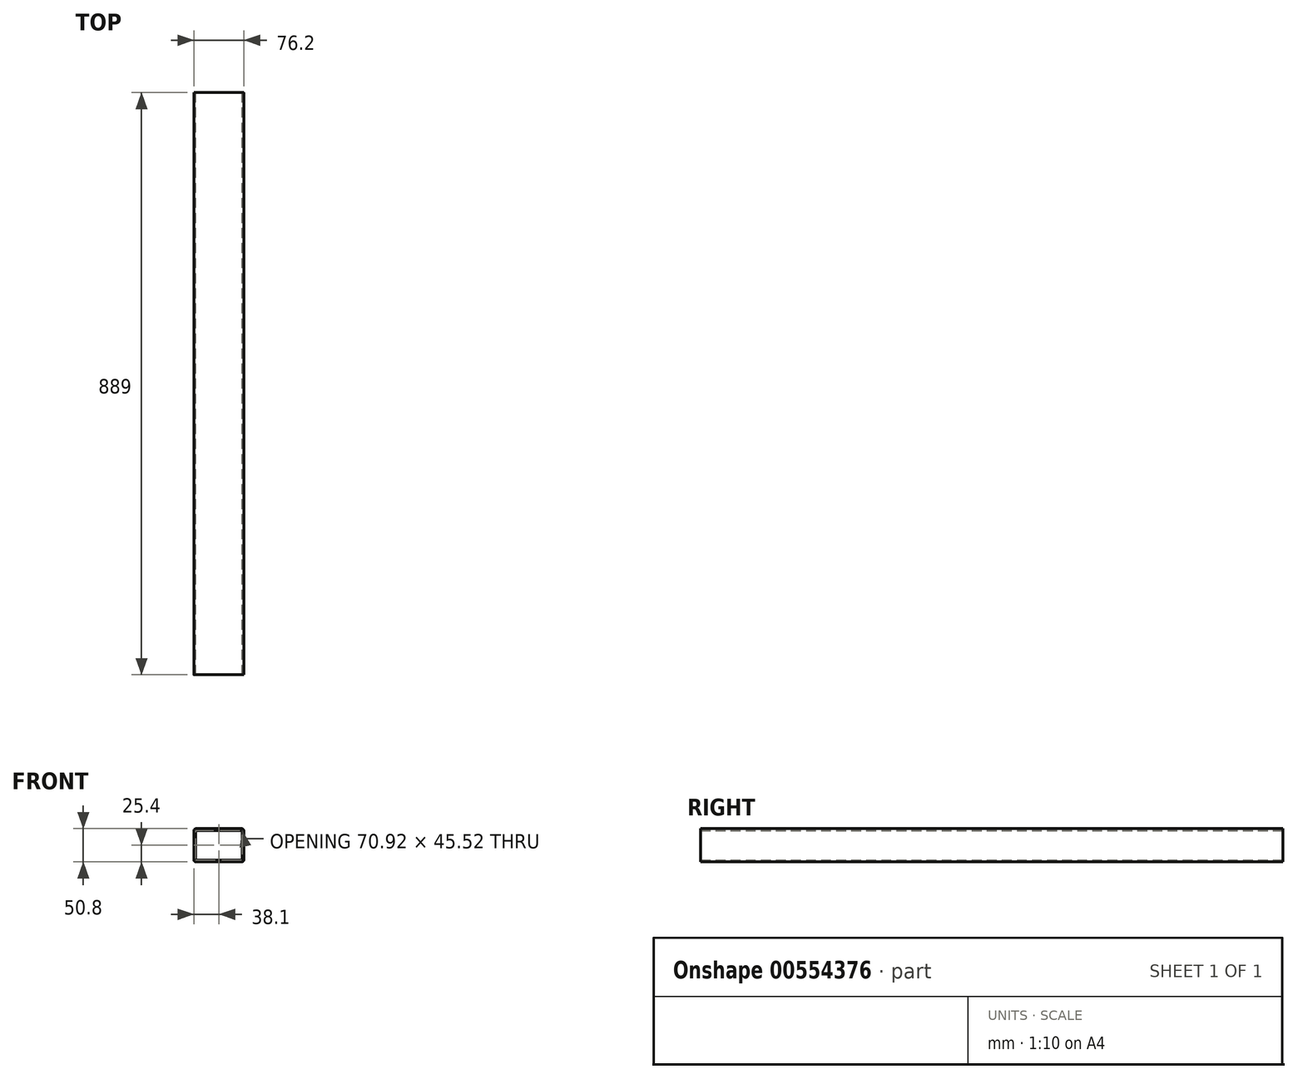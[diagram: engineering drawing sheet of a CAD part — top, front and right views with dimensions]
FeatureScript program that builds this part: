
annotation { "Feature Type Name" : "Feature", "Feature Type Description" : "" }
export const myFeature = defineFeature(function(context is Context, id is Id, definition is map)
    precondition{}
    {
        {
            var Q0;
            Q0=qCreatedBy(makeId("Front.planeOp"),FACE);
            var sketch = newSketch(context, id + "F0", { "sketchPlane" : qUnion([Q0])});
            skLineSegment(sketch, "E0.bottom", {"start": v(38.1, 25.4) * mm, "end": v(-38.1, 25.4) * mm});
            skLineSegment(sketch, "E0.top", {"start": v(38.1, -25.4) * mm, "end": v(-38.1, -25.4) * mm});
            skLineSegment(sketch, "E0.left", {"start": v(38.1, 25.4) * mm, "end": v(38.1, -25.4) * mm});
            skLineSegment(sketch, "E0.right", {"start": v(-38.1, 25.4) * mm, "end": v(-38.1, -25.4) * mm});
            skPoint(sketch, "E0.middle", {"position": v(0, 0) * mm});
            skLineSegment(sketch, "E1.bottom", {"start": v(35.46, 22.76) * mm, "end": v(-35.46, 22.76) * mm});
            skLineSegment(sketch, "E1.top", {"start": v(35.46, -22.76) * mm, "end": v(-35.46, -22.76) * mm});
            skLineSegment(sketch, "E1.left", {"start": v(35.46, 22.76) * mm, "end": v(35.46, -22.76) * mm});
            skLineSegment(sketch, "E1.right", {"start": v(-35.46, 22.76) * mm, "end": v(-35.46, -22.76) * mm});
            skSolve(sketch);
        }
        {
            var Q0;
            Q0 = qSketchRegion(id + "F0", true);
            extrude(context, id + "F1", {"entities" : qUnion([Q0]), "depth" : 889 * mm, "offsetDistance" : 25.4 * mm});
        }
        {
            var Q0;
            Q0=makeQuery(id+"F1.opExtrude","SWEPT_EDGE",EDGE,{"disambiguationData":[OSD([sQuery(id+"F0.wireOp",EDGE,"E0.bottom"),sQuery(id+"F0.wireOp",EDGE,"E0.left")])]});
            var Q1;
            Q1=makeQuery(id+"F1.opExtrude","SWEPT_EDGE",EDGE,{"disambiguationData":[OSD([sQuery(id+"F0.wireOp",EDGE,"E0.bottom"),sQuery(id+"F0.wireOp",EDGE,"E0.right")])]});
            var Q2;
            Q2=makeQuery(id+"F1.opExtrude","SWEPT_EDGE",EDGE,{"disambiguationData":[OSD([sQuery(id+"F0.wireOp",EDGE,"E1.top"),sQuery(id+"F0.wireOp",EDGE,"E1.right")])]});
            var Q3;
            Q3=makeQuery(id+"F1.opExtrude","SWEPT_EDGE",EDGE,{"disambiguationData":[OSD([sQuery(id+"F0.wireOp",EDGE,"E0.top"),sQuery(id+"F0.wireOp",EDGE,"E0.left")])]});
            var Q4;
            Q4=makeQuery(id+"F1.opExtrude","SWEPT_EDGE",EDGE,{"disambiguationData":[OSD([sQuery(id+"F0.wireOp",EDGE,"E0.top"),sQuery(id+"F0.wireOp",EDGE,"E0.right")])]});
            var Q5;
            Q5=makeQuery(id+"F1.opExtrude","SWEPT_EDGE",EDGE,{"disambiguationData":[OSD([sQuery(id+"F0.wireOp",EDGE,"E1.bottom"),sQuery(id+"F0.wireOp",EDGE,"E1.left")])]});
            var Q6;
            Q6=makeQuery(id+"F1.opExtrude","SWEPT_EDGE",EDGE,{"disambiguationData":[OSD([sQuery(id+"F0.wireOp",EDGE,"E1.top"),sQuery(id+"F0.wireOp",EDGE,"E1.left")])]});
            var Q7;
            Q7=makeQuery(id+"F1.opExtrude","SWEPT_EDGE",EDGE,{"disambiguationData":[OSD([sQuery(id+"F0.wireOp",EDGE,"E1.bottom"),sQuery(id+"F0.wireOp",EDGE,"E1.right")])]});
            fillet(context, id + "F2", {"entities" : qUnion([Q0, Q1, Q2, Q3, Q4, Q5, Q6, Q7]), "radius" : 3.17 * mm, "tangentPropagation" : true, "allowEdgeOverflow" : false});
        }
    });
